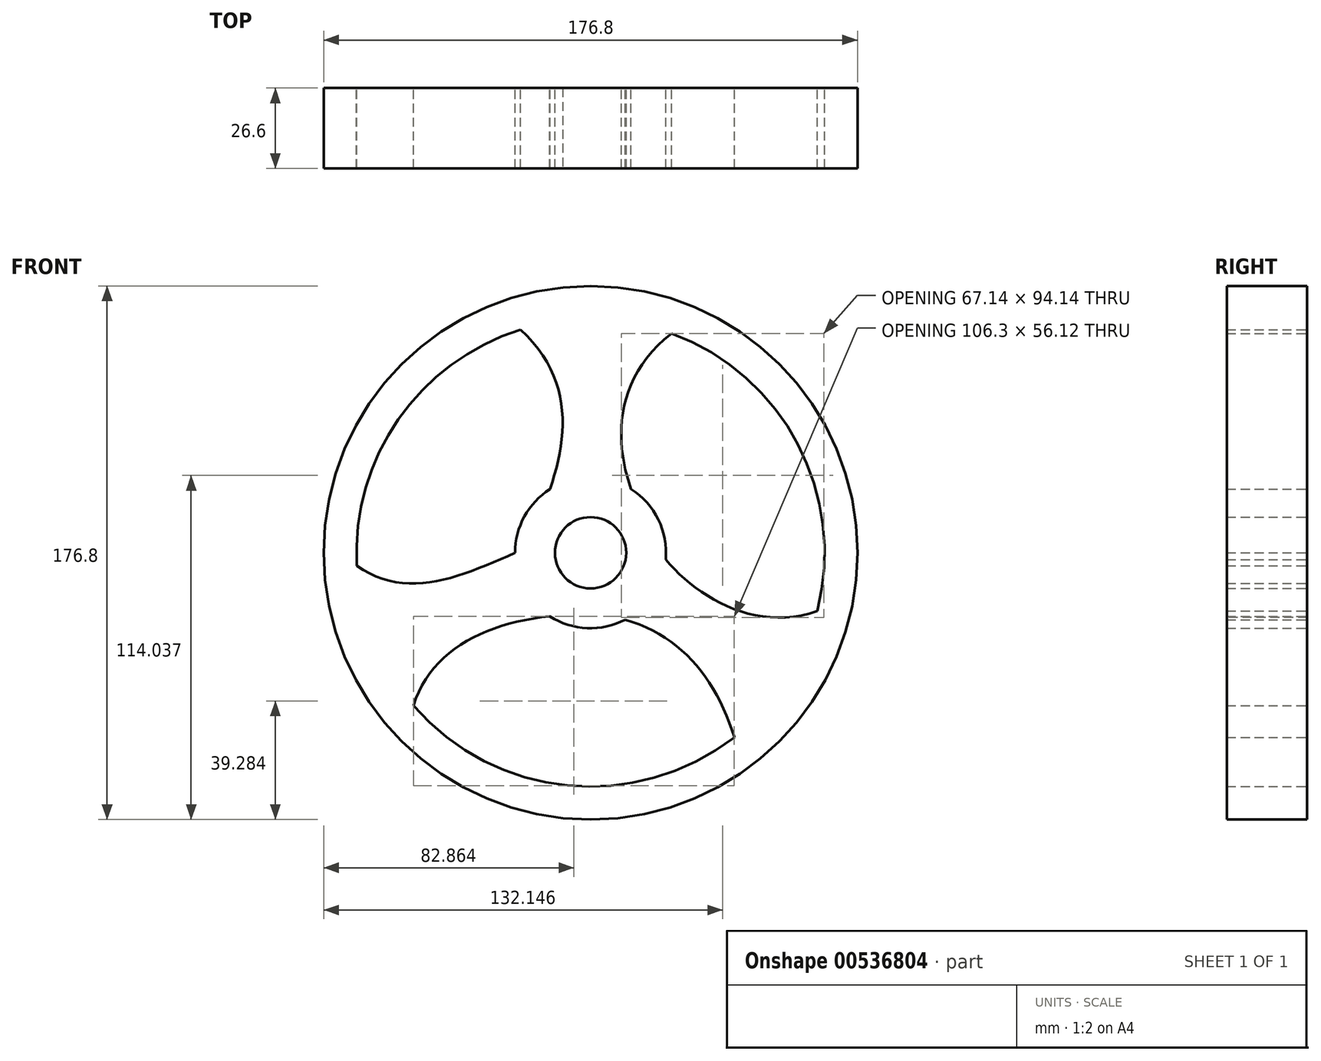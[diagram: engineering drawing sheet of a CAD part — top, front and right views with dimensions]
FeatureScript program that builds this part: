
annotation { "Feature Type Name" : "Feature", "Feature Type Description" : "" }
export const myFeature = defineFeature(function(context is Context, id is Id, definition is map)
    precondition{}
    {
        {
            var Q0;
            Q0=qCreatedBy(makeId("Front.planeOp"),FACE);
            var sketch = newSketch(context, id + "F0", { "sketchPlane" : qUnion([Q0])});
            skCircle(sketch, "E0", {"center": v(0, 0) * mm, "radius": 88.4 * mm});
            skCircle(sketch, "E1", {"center": v(0, 0) * mm, "radius": 77.5 * mm});
            skCircle(sketch, "E2", {"center": v(0, 0) * mm, "radius": 85.1 * mm});
            skCircle(sketch, "E3", {"center": v(0, 0) * mm, "radius": 25 * mm});
            skCircle(sketch, "E4", {"center": v(0, 0) * mm, "radius": 11.8 * mm});
            skFitSpline(sketch, "E5", {"points": [v(11.52, -22.19) * mm, v(47.61, -61.15) * mm], "startDerivative": vector(55.58, -15.7) * mm, "endDerivative": vector(17.65, -57.2) * mm});
            skFitSpline(sketch, "E6", {"points": [v(24.9, -2.26) * mm, v(75.05, -19.35) * mm], "startDerivative": vector(31.31, -37.4) * mm, "endDerivative": vector(60.63, 21.33) * mm});
            skFitSpline(sketch, "E7", {"points": [v(13.44, 21.08) * mm, v(26.84, 72.7) * mm], "startDerivative": vector(-17.17, 48.15) * mm, "endDerivative": vector(56.78, 43.63) * mm});
            skFitSpline(sketch, "E8", {"points": [v(-13.48, -21.05) * mm, v(-58.69, -50.62) * mm], "startDerivative": vector(-65.19, -6.75) * mm, "endDerivative": vector(-17.55, -54.5) * mm});
            skFitSpline(sketch, "E9", {"points": [v(-25, 0) * mm, v(-77.38, -4.25) * mm], "startDerivative": vector(-56.01, -25.03) * mm, "endDerivative": vector(-48.22, 34.73) * mm});
            skFitSpline(sketch, "E10", {"points": [v(-13.44, 21.08) * mm, v(-23.16, 73.96) * mm], "startDerivative": vector(18.46, 53.86) * mm, "endDerivative": vector(-51.54, 47.6) * mm});
            skSolve(sketch);
        }
        {
            var Q0;
            Q0 = qSketchRegion(id + "F0", true);
            var Q1;
            {var subQ0=sQuery(id+"F0.wireOp",EDGE,"E7");Q1=makeQuery(id+"F0.imprint","IMPRINT",FACE,{"disambiguationData":[TD([[makeQuery(id+"F0.imprint","IMPRINT",EDGE,{"derivedFrom":subQ0}),1.0]])]});}
            var Q2;
            {var subQ0=sQuery(id+"F0.wireOp",EDGE,"E5");Q2=makeQuery(id+"F0.imprint","IMPRINT",FACE,{"disambiguationData":[TD([[makeQuery(id+"F0.imprint","IMPRINT",EDGE,{"derivedFrom":subQ0}),1.0]])]});}
            var Q3;
            {var subQ0=sQuery(id+"F0.wireOp",EDGE,"E8");Q3=makeQuery(id+"F0.imprint","IMPRINT",FACE,{"disambiguationData":[TD([[makeQuery(id+"F0.imprint","IMPRINT",EDGE,{"derivedFrom":subQ0}),-1.0]])]});}
            var Q4;
            Q4=makeQuery(id+"F0.imprint","IMPRINT",FACE,{"disambiguationData":[TD([[makeQuery(id+"F0.imprint","IMPRINT",EDGE,{"derivedFrom":sQuery(id+"F0.wireOp",EDGE,"E2")}),1.0]])]});
            var Q5;
            Q5=makeQuery(id+"F0.imprint","IMPRINT",FACE,{"disambiguationData":[TD([[makeQuery(id+"F0.imprint","IMPRINT",EDGE,{"derivedFrom":sQuery(id+"F0.wireOp",EDGE,"E4")}),-1.0]])]});
            extrude(context, id + "F1", {"entities" : qUnion([Q0, Q1, Q2, Q3, Q4, Q5]), "endBound" : BoundingType.SYMMETRIC, "depth" : 26.6 * mm, "offsetDistance" : 25 * mm});
        }
    });
